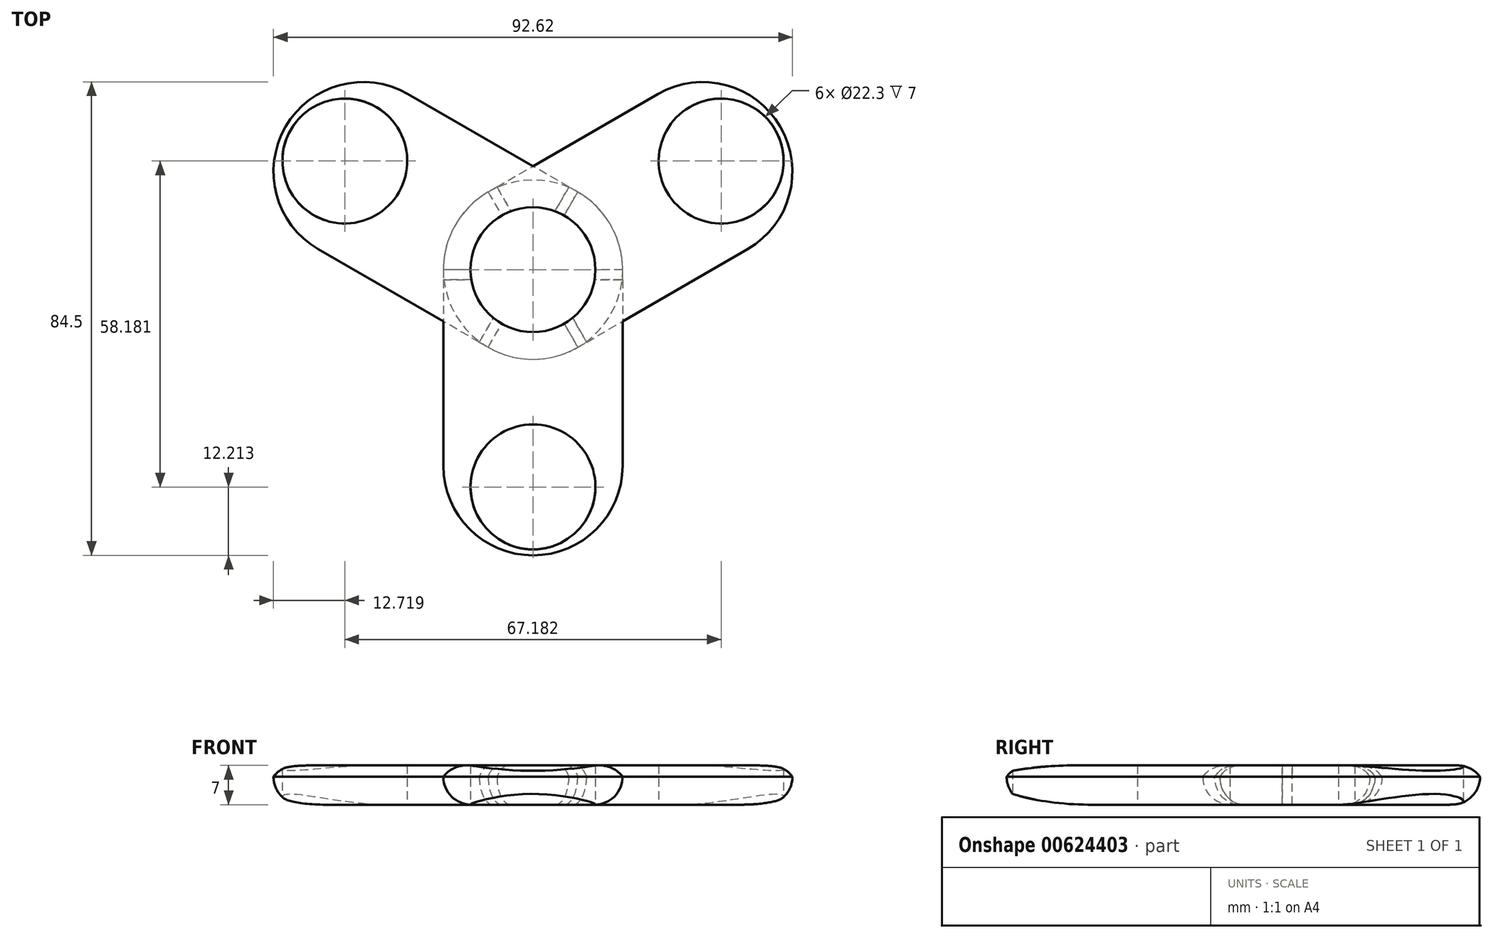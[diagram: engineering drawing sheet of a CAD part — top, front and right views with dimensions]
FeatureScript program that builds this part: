
annotation { "Feature Type Name" : "Feature", "Feature Type Description" : "" }
export const myFeature = defineFeature(function(context is Context, id is Id, definition is map)
    precondition{}
    {
        {
            var Q0;
            Q0=qCreatedBy(makeId("Top.planeOp"),FACE);
            var sketch = newSketch(context, id + "F0", { "sketchPlane" : qUnion([Q0])});
            skCircle(sketch, "E0", {"center": v(0, 0) * mm, "radius": 16 * mm});
            skCircle(sketch, "E1", {"center": v(0, -35) * mm, "radius": 16 * mm});
            skLineSegment(sketch, "E2", {"start": v(-16, 0) * mm, "end": v(-16, -35) * mm});
            skLineSegment(sketch, "E3", {"start": v(16, 0) * mm, "end": v(16, -35) * mm});
            skSolve(sketch);
        }
        {
            var Q0;
            Q0 = qSketchRegion(id + "F0", true);
            extrude(context, id + "F1", {"entities" : qUnion([Q0]), "depth" : 7 * mm, "offsetDistance" : 25 * mm});
        }
        {
            var Q0;
            Q0=qCreatedBy(makeId("Top.planeOp"),FACE);
            var sketch = newSketch(context, id + "F2", { "sketchPlane" : qUnion([Q0])});
            skCircle(sketch, "E4", {"center": v(0, 0) * mm, "radius": 11.15 * mm});
            skCircle(sketch, "E5", {"center": v(0, -38.79) * mm, "radius": 11.15 * mm});
            skSolve(sketch);
        }
        {
            var Q0;
            Q0 = qSketchRegion(id + "F2", true);
            extrude(context, id + "F3", {"entities" : qUnion([Q0]), "operationType" : NewBodyOperationType.REMOVE, "depth" : 7 * mm, "offsetDistance" : 25 * mm});
        }
        {
            var Q0;
            Q0=qCreatedBy(makeId("Front.planeOp"),FACE);
            var sketch = newSketch(context, id + "F4", { "sketchPlane" : qUnion([Q0])});
            skLineSegment(sketch, "E6", {"start": v(0, 0) * mm, "end": v(0, 35.28) * mm});
            skSolve(sketch);
        }
        {
            var Q0;
            Q0=makeQuery(id+"F1.opExtrude","SWEPT_BODY",BODY,{"disambiguationData":[OSD([sQuery(id+"F0.wireOp",EDGE,"E0"),sQuery(id+"F0.wireOp",EDGE,"E1"),sQuery(id+"F0.wireOp",EDGE,"E2"),sQuery(id+"F0.wireOp",EDGE,"E3")])]});
            var Q1;
            Q1=sQuery(id+"F4.wireOp",EDGE,"E6");
            circularPattern(context, id + "F5", {"entities" : qUnion([Q0]), "axis" : qUnion([Q1]), "angle" : 360 * degree, "instanceCount" : 3, "equalSpace" : true});
        }
        {
            var Q0;
            Q0=makeQuery(id+"F1.opExtrude","CAP_EDGE",EDGE,{"disambiguationData":[OSD([sQuery(id+"F0.wireOp",EDGE,"E2")])],"isStart":true});
            fillet(context, id + "F6", {"entities" : qUnion([Q0]), "radius" : 5 * mm, "tangentPropagation" : true, "allowEdgeOverflow" : false});
        }
        {
            var Q0;
            Q0=makeQuery(id+"F5.opPattern","COPY",EDGE,{"derivedFrom":makeQuery(id+"F1.opExtrude","CAP_EDGE",EDGE,{"disambiguationData":[OSD([sQuery(id+"F0.wireOp",EDGE,"E2")])],"isStart":true}),"instanceName":"1"});
            fillet(context, id + "F7", {"entities" : qUnion([Q0]), "radius" : 5 * mm, "tangentPropagation" : true, "allowEdgeOverflow" : false});
        }
        {
            var Q0;
            Q0=makeQuery(id+"F5.opPattern","COPY",EDGE,{"derivedFrom":makeQuery(id+"F1.opExtrude","CAP_EDGE",EDGE,{"disambiguationData":[OSD([sQuery(id+"F0.wireOp",EDGE,"E2")])],"isStart":true}),"instanceName":"2"});
            fillet(context, id + "F8", {"entities" : qUnion([Q0]), "radius" : 5 * mm, "tangentPropagation" : true, "allowEdgeOverflow" : false});
        }
        {
            var Q0;
            Q0=makeQuery(id+"F1.opExtrude","CAP_EDGE",EDGE,{"disambiguationData":[OSD([sQuery(id+"F0.wireOp",EDGE,"E3")])],"isStart":false});
            fillet(context, id + "F9", {"entities" : qUnion([Q0]), "radius" : 5 * mm, "tangentPropagation" : true, "allowEdgeOverflow" : false});
        }
        {
            var Q0;
            Q0=makeQuery(id+"F5.opPattern","COPY",EDGE,{"derivedFrom":makeQuery(id+"F1.opExtrude","CAP_EDGE",EDGE,{"disambiguationData":[OSD([sQuery(id+"F0.wireOp",EDGE,"E2")])],"isStart":false}),"instanceName":"1"});
            fillet(context, id + "F10", {"entities" : qUnion([Q0]), "radius" : 5 * mm, "tangentPropagation" : true, "allowEdgeOverflow" : false});
        }
        {
            var Q0;
            Q0=makeQuery(id+"F5.opPattern","COPY",EDGE,{"derivedFrom":makeQuery(id+"F1.opExtrude","CAP_EDGE",EDGE,{"disambiguationData":[OSD([sQuery(id+"F0.wireOp",EDGE,"E2")])],"isStart":false}),"instanceName":"2"});
            fillet(context, id + "F11", {"entities" : qUnion([Q0]), "radius" : 5 * mm, "tangentPropagation" : true, "allowEdgeOverflow" : false});
        }
    });
